# Revit family: BORGE_Снегозадержатель трубчатый
name_source: partatom
category: Обобщенные модели
units: mm (PartAtom-declared; Revit-internal decimal feet)

## family parameters
Всегда вертикально = Нет
Заголовок OmniClass = Diffusers, Registers, and Grilles
Может служить основой для арматурных стержней = Нет
На основе рабочей плоскости = Да
Номер OmniClass = 23.75.70.21.27.11
Общий = Нет
При загрузке вырезать с полостями = Нет
Размер круглого соединителя = Использовать диаметр
Тип детали = Нормальный
Точка расчета площади = Да

## types (44) — shared parameters
ADSK_URL документации изделия = https://borge.ru
ADSK_URL страницы изделия = https://borge.pro
ADSK_Версия семейства = Rev1 2023-08
BIM Support_Разрабочик = BIM Support
BIM Support_Сайт = https://www.bim-support.ru
LT = BORGE_Снегозадержатель_Трубчатый
URL = https://borge.ru
Изготовитель = ООО «Борге», ООО «Бипро»
zero-valued in all types: Отметка по умолчанию

## per-type parameters (varying)
| type | ADSK_Материал | BORGE_Единица измерения_м | BORGE_Единица измерения_шт | Code1 | Code2 | Kr_3_4_Vis |
| Снегозадержатель трубчатый_1.5 м_Бело-алюминиевый_RAL 9006 | BOGRE_Уcловный_Бело-алюминиевый_RAL 9006 | Нет | Да | 1 | 1 | Нет |
| Снегозадержатель трубчатый_1.5 м_Чёрный матовый_RAL 9005 | BOGRE_Уcловный_Чёрный матовый_RAL 9005 | Нет | Да | 1 | 2 | Нет |
| Снегозадержатель трубчатый_1.5 м_Чёрный_RAL 9005 | BOGRE_Уcловный_Чёрный_RAL 9005 | Нет | Да | 1 | 3 | Нет |
| Снегозадержатель трубчатый_1.5 м_Сигнально-белый_RAL 9003 | BOGRE_Уcловный_Сигнально-белый_RAL 9003 | Нет | Да | 1 | 4 | Нет |
| Снегозадержатель трубчатый_1.5 м_Окрашенный_NL 807 | BOGRE_Уcловный_Окрашенный_NL 807 | Нет | Да | 1 | 5 | Нет |
| Снегозадержатель трубчатый_1.5 м_Окрашенный_NL 805 | BOGRE_Уcловный_Окрашенный_NL 805 | Нет | Да | 1 | 6 | Нет |
| Снегозадержатель трубчатый_1.5 м_Серо-коричневый матовый_RAL 8019 | BOGRE_Уcловный_Серо-коричневый матовый_RAL 8019 | Нет | Да | 1 | 7 | Нет |
| Снегозадержатель трубчатый_1.5 м_Серо-коричневый_RAL 8019 | BOGRE_Уcловный_Серо-коричневый_RAL 8019 | Нет | Да | 1 | 8 | Нет |
| Снегозадержатель трубчатый_1.5 м_Коричневый шоколад матовый_RAL 8017 | BOGRE_Уcловный_Коричневый шоколад матовый_RAL 8017 | Нет | Да | 1 | 9 | Нет |
| Снегозадержатель трубчатый_1.5 м_Коричневый шоколад_RAL 8017 | BOGRE_Уcловный_Коричневый шоколад_RAL 8017 | Нет | Да | 1 | 10 | Нет |
| Снегозадержатель трубчатый_1.5 м_Терракотовый_RAL 8004 | BOGRE_Уcловный_Терракотовый_RAL 8004 | Нет | Да | 1 | 11 | Нет |
| Снегозадержатель трубчатый_1.5 м_Серый графит матовый_RAL 7024 | BOGRE_Уcловный_Серый графит матовый_RAL 7024 | Нет | Да | 1 | 12 | Нет |
| Снегозадержатель трубчатый_1.5 м_Серый графит_RAL 7024 | BOGRE_Уcловный_Серый графит_RAL 7024 | Нет | Да | 1 | 13 | Нет |
| Снегозадержатель трубчатый_1.5 м_Антрацитово-серый_RAL 7016 | BOGRE_Уcловный_Антрацитово-серый_RAL 7016 | Нет | Да | 1 | 14 | Нет |
| Снегозадержатель трубчатый_1.5 м_Сигнально-серый_RAL 7004 | BOGRE_Уcловный_Сигнально-серый_RAL 7004 | Нет | Да | 1 | 15 | Нет |
| Снегозадержатель трубчатый_1.5 м_Зелёный мох_RAL 6005 | BOGRE_Уcловный_Зелёный мох_RAL 6005 | Нет | Да | 1 | 16 | Нет |
| Снегозадержатель трубчатый_1.5 м_Лиственно-зеленый_RAL 6002 | BOGRE_Уcловный_Лиственно-зеленый_RAL 6002 | Нет | Да | 1 | 17 | Нет |
| Снегозадержатель трубчатый_1.5 м_Сигнально-синий_RAL 5005 | BOGRE_Уcловный_Сигнально-синий_RAL 5005 | Нет | Да | 1 | 18 | Нет |
| Снегозадержатель трубчатый_1.5 м_Серо-коричневый_RR 32 | BOGRE_Уcловный_Серо-коричневый_RR 32 | Нет | Да | 1 | 19 | Нет |
| Снегозадержатель трубчатый_1.5 м_Коричнево-красный_RAL 3011 | BOGRE_Уcловный_Коричнево-красный_RAL 3011 | Нет | Да | 1 | 20 | Нет |
| Снегозадержатель трубчатый_1.5 м_Красное вино_RAL 3005 | BOGRE_Уcловный_Красное вино_RAL 3005 | Нет | Да | 1 | 21 | Нет |
| Снегозадержатель трубчатый_1.5 м_Рубиново-красный_RAL 3003 | BOGRE_Уcловный_Рубиново-красный_RAL 3003 | Нет | Да | 1 | 22 | Нет |
| Снегозадержатель трубчатый_3 м_Бело-алюминиевый_RAL 9006 | BOGRE_Уcловный_Бело-алюминиевый_RAL 9006 | Нет | Да | 2 | 23 | Да |
| Снегозадержатель трубчатый_3 м_Чёрный матовый_RAL 9005 | BOGRE_Уcловный_Чёрный матовый_RAL 9005 | Нет | Да | 2 | 24 | Да |
| Снегозадержатель трубчатый_3 м_Чёрный_RAL 9005 | BOGRE_Уcловный_Чёрный_RAL 9005 | Нет | Да | 2 | 25 | Да |
| Снегозадержатель трубчатый_3 м_Сигнально-белый_RAL 9003 | BOGRE_Уcловный_Сигнально-белый_RAL 9003 | Нет | Да | 2 | 26 | Да |
| Снегозадержатель трубчатый_3 м_Окрашенный_NL 807 | BOGRE_Уcловный_Окрашенный_NL 807 | Нет | Да | 2 | 27 | Да |
| Снегозадержатель трубчатый_3 м_Окрашенный_NL 805 | BOGRE_Уcловный_Окрашенный_NL 805 | Нет | Да | 2 | 28 | Да |
| Снегозадержатель трубчатый_3 м_Серо-коричневый матовый_RAL 8019 | BOGRE_Уcловный_Серо-коричневый матовый_RAL 8019 | Нет | Да | 2 | 29 | Да |
| Снегозадержатель трубчатый_3 м_Серо-коричневый_RAL 8019 | BOGRE_Уcловный_Серо-коричневый_RAL 8019 | Нет | Да | 2 | 30 | Да |
| Снегозадержатель трубчатый_3 м_Коричневый шоколад матовый_RAL 8017 | BOGRE_Уcловный_Коричневый шоколад матовый_RAL 8017 | Нет | Да | 2 | 31 | Да |
| Снегозадержатель трубчатый_3 м_Коричневый шоколад_RAL 8017 | BOGRE_Уcловный_Коричневый шоколад_RAL 8017 | Нет | Да | 2 | 32 | Да |
| Снегозадержатель трубчатый_3 м_Терракотовый_RAL 8004 | BOGRE_Уcловный_Терракотовый_RAL 8004 | Нет | Да | 2 | 33 | Да |
| Снегозадержатель трубчатый_3 м_Серый графит матовый_RAL 7024 | BOGRE_Уcловный_Серый графит матовый_RAL 7024 | Нет | Да | 2 | 34 | Да |
| Снегозадержатель трубчатый_3 м_Серый графит_RAL 7024 | BOGRE_Уcловный_Серый графит_RAL 7024 | Нет | Да | 2 | 35 | Да |
| Снегозадержатель трубчатый_3 м_Антрацитово-серый_RAL 7016 | BOGRE_Уcловный_Антрацитово-серый_RAL 7016 | Нет | Да | 2 | 36 | Да |
| Снегозадержатель трубчатый_3 м_Сигнально-серый_RAL 7004 | BOGRE_Уcловный_Сигнально-серый_RAL 7004 | Нет | Да | 2 | 37 | Да |
| Снегозадержатель трубчатый_3 м_Зелёный мох_RAL 6005 | BOGRE_Уcловный_Зелёный мох_RAL 6005 | Нет | Да | 2 | 38 | Да |
| Снегозадержатель трубчатый_3 м_Лиственно-зеленый_RAL 6002 | BOGRE_Уcловный_Лиственно-зеленый_RAL 6002 | Нет | Да | 2 | 39 | Да |
| Снегозадержатель трубчатый_3 м_Сигнально-синий_RAL 5005 | BOGRE_Уcловный_Сигнально-синий_RAL 5005 | Нет | Да | 2 | 40 | Да |
| Снегозадержатель трубчатый_3 м_Серо-коричневый_RR 32 | BOGRE_Уcловный_Серо-коричневый_RR 32 | Нет | Да | 2 | 41 | Да |
| Снегозадержатель трубчатый_3 м_Коричнево-красный_RAL 3011 | BOGRE_Уcловный_Коричнево-красный_RAL 3011 | Нет | Да | 2 | 42 | Да |
| Снегозадержатель трубчатый_3 м_Красное вино_RAL 3005 | BOGRE_Уcловный_Красное вино_RAL 3005 | Да | Нет | 2 | 43 | Да |
| Снегозадержатель трубчатый_3 м_Рубиново-красный_RAL 3003 | BOGRE_Уcловный_Рубиново-красный_RAL 3003 | Нет | Да | 2 | 44 | Да |
